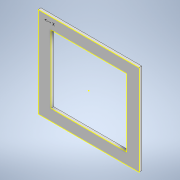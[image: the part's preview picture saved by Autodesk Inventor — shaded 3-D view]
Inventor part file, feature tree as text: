
AUTODESK INVENTOR PART (.ipt)
format: ipt  version: 2021 (Build 250183000, 183)  size: 107,520 bytes
history: native  units: mm
features: sketch x2, extrude x1, projected_geometry x1
ambient origin geometry x8: Origin, YZ Plane, XZ Plane, XY Plane, X Axis, Y Axis, Z Axis, Center Point
bodies: Solid1 (feature_tree)
feature tree (4):
  extrude  "Extrusion1"  Depth=150.0mm
  sketch  "Sketch2"  dims[d2=200.0mm d3=6.0mm d4=0.0mm]
  sketch  "Sketch1"  dims[d0=167.0mm d1=150.0mm]
  projected_geometry  "Projected Loop1"
